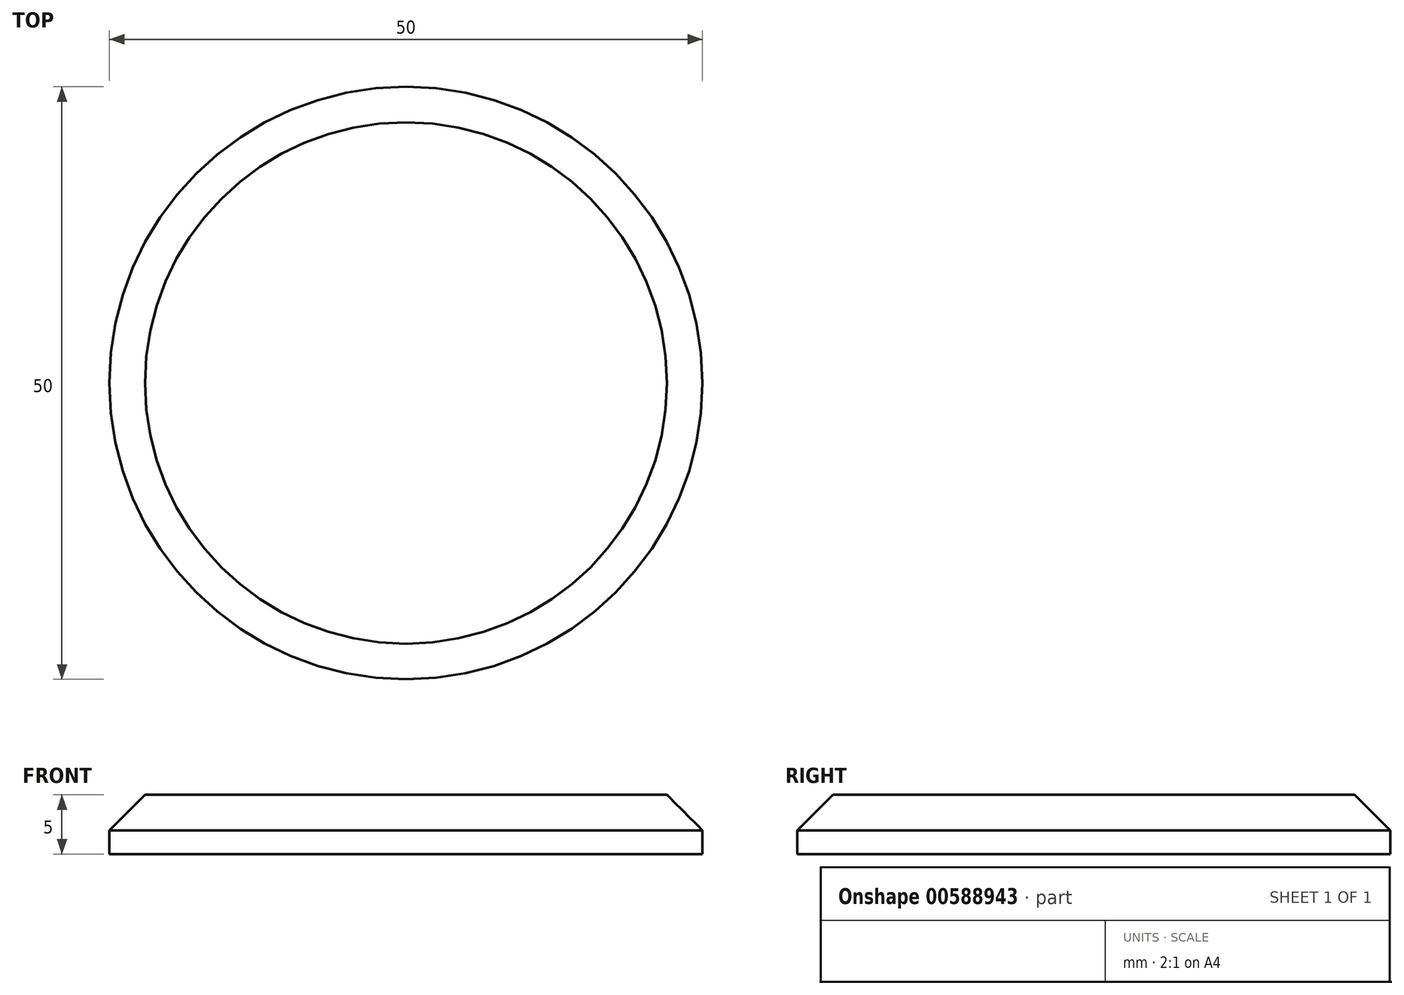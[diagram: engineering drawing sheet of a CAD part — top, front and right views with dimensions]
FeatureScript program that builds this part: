
annotation { "Feature Type Name" : "Feature", "Feature Type Description" : "" }
export const myFeature = defineFeature(function(context is Context, id is Id, definition is map)
    precondition{}
    {
        {
            var Q0;
            Q0=qCreatedBy(makeId("Top.planeOp"),FACE);
            var sketch = newSketch(context, id + "F0", { "sketchPlane" : qUnion([Q0])});
            skCircle(sketch, "E0", {"center": v(0, 0) * mm, "radius": 25 * mm});
            skSolve(sketch);
        }
        {
            var Q0;
            Q0=makeQuery(id+"F0.imprint","IMPRINT",FACE,{"disambiguationData":[TD([[makeQuery(id+"F0.imprint","IMPRINT",EDGE,{"derivedFrom":sQuery(id+"F0.wireOp",EDGE,"E0")}),1.0]])]});
            extrude(context, id + "F1", {"entities" : qUnion([Q0]), "depth" : 5 * mm, "offsetDistance" : 25 * mm});
        }
        {
            var Q0;
            Q0=makeQuery(id+"F1.opExtrude","CAP_EDGE",EDGE,{"disambiguationData":[OSD([sQuery(id+"F0.wireOp",EDGE,"E0")])],"isStart":false});
            chamfer(context, id + "F2", {"entities" : qUnion([Q0]), "width" : 3 * mm, "tangentPropagation" : true});
        }
    });
